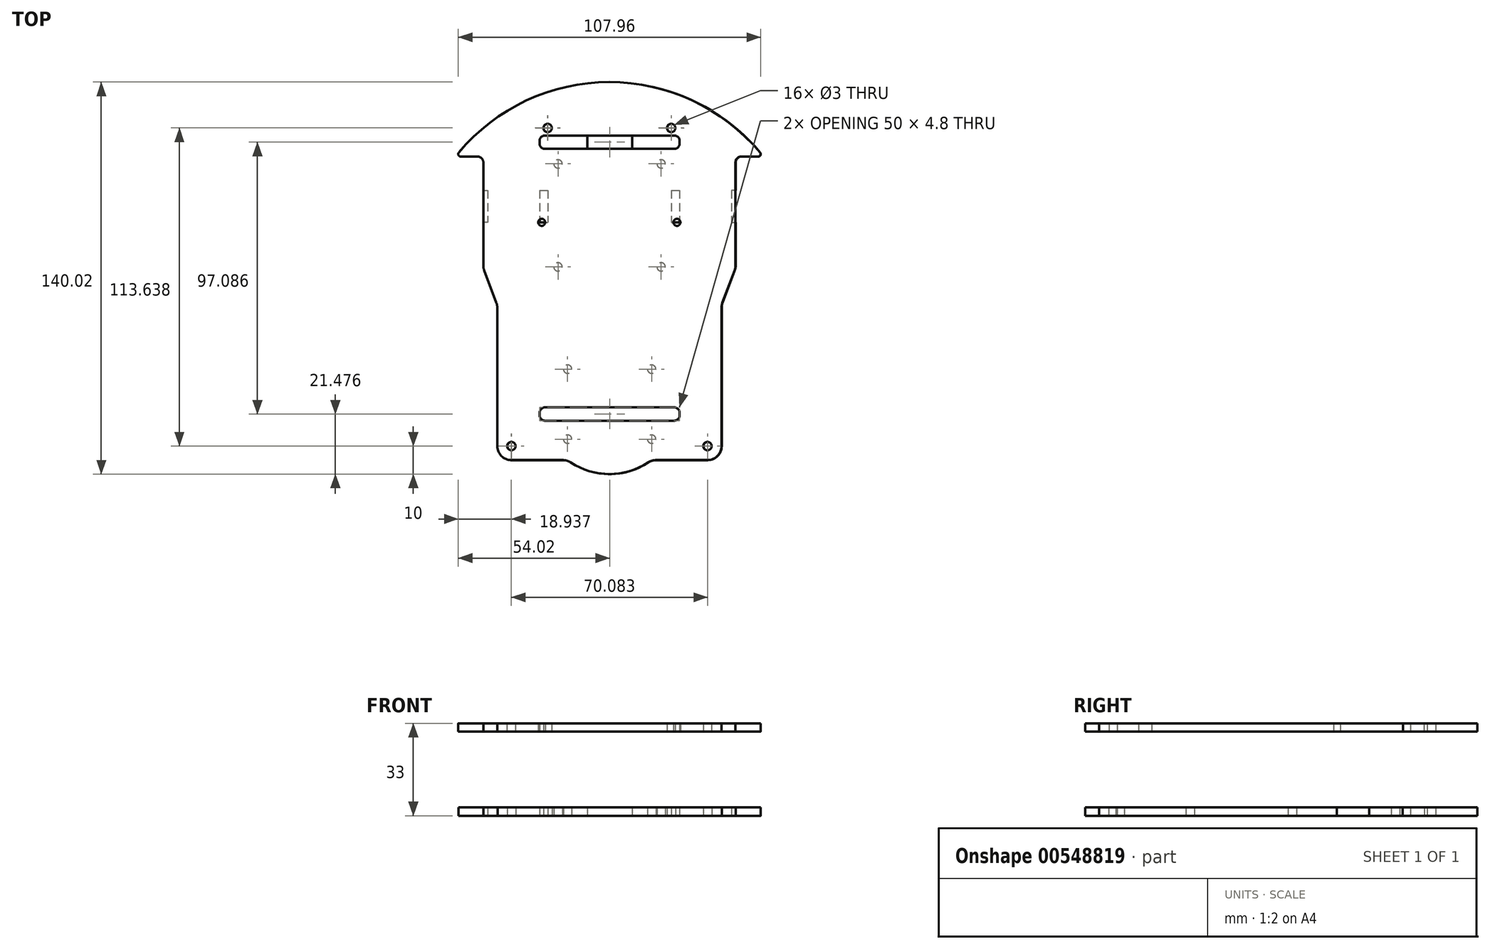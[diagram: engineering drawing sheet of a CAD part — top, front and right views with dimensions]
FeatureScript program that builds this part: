
annotation { "Feature Type Name" : "Feature", "Feature Type Description" : "" }
export const myFeature = defineFeature(function(context is Context, id is Id, definition is map)
    precondition{}
    {
        {
            var Q0;
            Q0=qCreatedBy(makeId("Top.planeOp"),FACE);
            var sketch = newSketch(context, id + "F0", { "sketchPlane" : qUnion([Q0])});
            skArc(sketch, "E0", {"start": v(53.73, 44.87) * mm, "mid": v(0, 70) * mm, "end": v(-53.73, 44.87) * mm});
            skLineSegment(sketch, "E1", {"start": v(-45, 71.35) * mm, "end": v(-45, 53.62) * mm, "construction": true});
            skLineSegment(sketch, "E2", {"start": v(-44.93, -66.83) * mm, "end": v(45.07, -66.83) * mm, "construction": true});
            skLineSegment(sketch, "E3", {"start": v(45, 4.53) * mm, "end": v(45, 19.9) * mm, "construction": true});
            skArc(sketch, "E4", {"start": v(-13.82, -65.83) * mm, "mid": v(0, -70) * mm, "end": v(13.82, -65.83) * mm});
            skLineSegment(sketch, "E5", {"start": v(-45, 53.62) * mm, "end": v(45, 53.62) * mm, "construction": true});
            skLineSegment(sketch, "E6", {"start": v(84.91, 3.62) * mm, "end": v(-92.34, 3.62) * mm, "construction": true});
            skLineSegment(sketch, "E7", {"start": v(-54.93, 66.8) * mm, "end": v(-54.93, -70.54) * mm, "construction": true});
            skLineSegment(sketch, "E8", {"start": v(55, 69.5) * mm, "end": v(55, -68.16) * mm, "construction": true});
            skLineSegment(sketch, "E9", {"start": v(-53.04, 43.4) * mm, "end": v(-47, 43.4) * mm});
            skLineSegment(sketch, "E10", {"start": v(-44.68, 2.77) * mm, "end": v(-40.32, -8.82) * mm});
            skLineSegment(sketch, "E11", {"start": v(40.32, -8.82) * mm, "end": v(44.68, 2.77) * mm});
            skLineSegment(sketch, "E12", {"start": v(45, 43.4) * mm, "end": v(45, 31.4) * mm});
            skLineSegment(sketch, "E13", {"start": v(-45, 3.62) * mm, "end": v(-45, 19.9) * mm});
            skLineSegment(sketch, "E14.trimOffspring", {"start": v(47, 43.4) * mm, "end": v(53.04, 43.4) * mm});
            skLineSegment(sketch, "E15.trimOffspring", {"start": v(-45, 41.4) * mm, "end": v(-45, 31.4) * mm, "construction": true});
            skLineSegment(sketch, "E16", {"start": v(68.52, 31.4) * mm, "end": v(-73.16, 31.4) * mm, "construction": true});
            skLineSegment(sketch, "E17", {"start": v(-80.27, 19.9) * mm, "end": v(70.38, 19.9) * mm, "construction": true});
            skLineSegment(sketch, "E18", {"start": v(-43.5, 37.52) * mm, "end": v(-43.5, 12.77) * mm, "construction": true});
            skLineSegment(sketch, "E19", {"start": v(43.5, 37.52) * mm, "end": v(43.5, 11.84) * mm, "construction": true});
            skLineSegment(sketch, "E20", {"start": v(-45, 31.4) * mm, "end": v(-43.5, 31.4) * mm});
            skLineSegment(sketch, "E21", {"start": v(-43.5, 31.4) * mm, "end": v(-43.5, 19.9) * mm});
            skLineSegment(sketch, "E22", {"start": v(-43.5, 19.9) * mm, "end": v(-45, 19.9) * mm});
            skLineSegment(sketch, "E23.trimOffspring", {"start": v(-45, 19.9) * mm, "end": v(-45, 4.53) * mm, "construction": true});
            skLineSegment(sketch, "E24.trimOffspring", {"start": v(-45, 31.4) * mm, "end": v(-45, 43.4) * mm});
            skLineSegment(sketch, "E25", {"start": v(45, 31.4) * mm, "end": v(43.5, 31.4) * mm});
            skLineSegment(sketch, "E26", {"start": v(43.5, 31.4) * mm, "end": v(43.5, 19.9) * mm});
            skLineSegment(sketch, "E27", {"start": v(43.5, 19.9) * mm, "end": v(45, 19.9) * mm});
            skLineSegment(sketch, "E28.trimOffspring", {"start": v(45, 31.4) * mm, "end": v(45, 41.4) * mm, "construction": true});
            skLineSegment(sketch, "E29.trimOffspring", {"start": v(45, 19.9) * mm, "end": v(45, 3.62) * mm});
            skLineSegment(sketch, "E30", {"start": v(-24.9, 37.4) * mm, "end": v(-24.9, 9.84) * mm, "construction": true});
            skPoint(sketch, "E30.startSnap0", {"position": v(-45, 37.4) * mm});
            skLineSegment(sketch, "E31", {"start": v(-24.9, 9.84) * mm, "end": v(24.9, 9.84) * mm, "construction": true});
            skLineSegment(sketch, "E32", {"start": v(24.9, 9.84) * mm, "end": v(24.9, 37.52) * mm, "construction": true});
            skLineSegment(sketch, "E33", {"start": v(-22, 37.06) * mm, "end": v(-22, 13.24) * mm, "construction": true});
            skLineSegment(sketch, "E34", {"start": v(-22, 13.24) * mm, "end": v(22, 13.24) * mm, "construction": true});
            skLineSegment(sketch, "E35", {"start": v(22, 13.24) * mm, "end": v(22, 38.3) * mm, "construction": true});
            skLineSegment(sketch, "E36.bottom", {"start": v(-24.9, 31.4) * mm, "end": v(-22, 31.4) * mm});
            skLineSegment(sketch, "E36.top", {"start": v(-24.9, 19.9) * mm, "end": v(-22, 19.9) * mm});
            skLineSegment(sketch, "E36.left", {"start": v(-24.9, 31.4) * mm, "end": v(-24.9, 19.9) * mm});
            skLineSegment(sketch, "E36.right", {"start": v(-22, 31.4) * mm, "end": v(-22, 19.9) * mm});
            skLineSegment(sketch, "E37.bottom", {"start": v(22, 31.4) * mm, "end": v(24.9, 31.4) * mm});
            skLineSegment(sketch, "E37.top", {"start": v(22, 19.9) * mm, "end": v(24.9, 19.9) * mm});
            skLineSegment(sketch, "E37.left", {"start": v(22, 31.4) * mm, "end": v(22, 19.9) * mm});
            skLineSegment(sketch, "E37.right", {"start": v(24.9, 31.4) * mm, "end": v(24.9, 19.9) * mm});
            skPoint(sketch, "E38.oppositeSnap0", {"position": v(22, 25.77) * mm});
            skLineSegment(sketch, "E38.left", {"start": v(22, 25.77) * mm, "end": v(22, 25.77) * mm});
            skLineSegment(sketch, "E38.right", {"start": v(-22, 25.77) * mm, "end": v(-22, 25.77) * mm});
            skLineSegment(sketch, "E39.bottom", {"start": v(-8, 51.14) * mm, "end": v(8, 51.14) * mm});
            skLineSegment(sketch, "E39.top", {"start": v(-8, 46.14) * mm, "end": v(8, 46.14) * mm});
            skLineSegment(sketch, "E39.left", {"start": v(-8, 51.14) * mm, "end": v(-8, 46.14) * mm});
            skLineSegment(sketch, "E39.right", {"start": v(8, 51.14) * mm, "end": v(8, 46.14) * mm});
            skCircle(sketch, "E40", {"center": v(18.4, 40.8) * mm, "radius": 1.5 * mm});
            skCircle(sketch, "E41.MirrorC", {"center": v(-18.4, 40.8) * mm, "radius": 1.5 * mm});
            skCircle(sketch, "E42", {"center": v(18.4, 4) * mm, "radius": 1.5 * mm});
            skLineSegment(sketch, "E43", {"start": v(18.4, 40.8) * mm, "end": v(18.4, -27.62) * mm, "construction": true});
            skCircle(sketch, "E44.MirrorC", {"center": v(-18.4, 4) * mm, "radius": 1.5 * mm});
            skLineSegment(sketch, "E45.top", {"start": v(-35, -65) * mm, "end": v(-16.58, -65) * mm});
            skLineSegment(sketch, "E45.left", {"start": v(-40, -10.58) * mm, "end": v(-40, -60) * mm});
            skLineSegment(sketch, "E45.right", {"start": v(40, -10.58) * mm, "end": v(40, -60) * mm});
            skLineSegment(sketch, "E46.trimOffspring", {"start": v(16.58, -65) * mm, "end": v(35, -65) * mm});
            skLineSegment(sketch, "E47", {"start": v(-63.48, 0) * mm, "end": v(68.67, 0) * mm, "construction": true});
            skPoint(sketch, "E48.visualSharp", {"position": v(-40, -65) * mm});
            skArc(sketch, "E48.filletArc", {"start": v(-40, -60) * mm, "mid": v(-38.54, -63.54) * mm, "end": v(-35, -65) * mm});
            skPoint(sketch, "E49.visualSharp", {"position": v(40, -65) * mm});
            skArc(sketch, "E49.filletArc", {"start": v(35, -65) * mm, "mid": v(38.54, -63.54) * mm, "end": v(40, -60) * mm});
            skPoint(sketch, "E50.visualSharp", {"position": v(15, -65) * mm});
            skArc(sketch, "E50.filletArc", {"start": v(16.58, -65) * mm, "mid": v(15.14, -65.21) * mm, "end": v(13.82, -65.83) * mm});
            skPoint(sketch, "E51.visualSharp", {"position": v(-15, -65) * mm});
            skArc(sketch, "E51.filletArc", {"start": v(-13.82, -65.83) * mm, "mid": v(-15.14, -65.21) * mm, "end": v(-16.58, -65) * mm});
            skArc(sketch, "E52.filletArc", {"start": v(-45, 4.53) * mm, "mid": v(-44.92, 3.63) * mm, "end": v(-44.68, 2.77) * mm});
            skArc(sketch, "E53.filletArc", {"start": v(44.68, 2.77) * mm, "mid": v(44.92, 3.63) * mm, "end": v(45, 4.53) * mm});
            skPoint(sketch, "E54.visualSharp", {"position": v(40, -9.67) * mm});
            skArc(sketch, "E54.filletArc", {"start": v(40.32, -8.82) * mm, "mid": v(40.08, -9.69) * mm, "end": v(40, -10.58) * mm});
            skPoint(sketch, "E55.visualSharp", {"position": v(-40, -9.67) * mm});
            skArc(sketch, "E55.filletArc", {"start": v(-40, -10.58) * mm, "mid": v(-40.08, -9.69) * mm, "end": v(-40.32, -8.82) * mm});
            skPoint(sketch, "E56.visualSharp", {"position": v(-54.93, 43.4) * mm});
            skArc(sketch, "E56.filletArc", {"start": v(-53.73, 44.87) * mm, "mid": v(-53.85, 43.91) * mm, "end": v(-53.04, 43.4) * mm});
            skPoint(sketch, "E57.visualSharp", {"position": v(54.93, 43.4) * mm});
            skArc(sketch, "E57.filletArc", {"start": v(53.04, 43.4) * mm, "mid": v(53.85, 43.91) * mm, "end": v(53.73, 44.87) * mm});
            skPoint(sketch, "E58.visualSharp", {"position": v(-45, 43.4) * mm});
            skArc(sketch, "E58.filletArc", {"start": v(-45, 41.4) * mm, "mid": v(-45.59, 42.8) * mm, "end": v(-47, 43.4) * mm});
            skArc(sketch, "E59.filletArc", {"start": v(47, 43.4) * mm, "mid": v(45.59, 42.8) * mm, "end": v(45, 41.4) * mm});
            skCircle(sketch, "E60", {"center": v(-35, -60) * mm, "radius": 1.5 * mm});
            skCircle(sketch, "E61.MirrorC", {"center": v(35, -60) * mm, "radius": 1.5 * mm});
            skCircle(sketch, "E62", {"center": v(-22.05, 53.62) * mm, "radius": 1.5 * mm});
            skCircle(sketch, "E63.MirrorC", {"center": v(22.05, 53.62) * mm, "radius": 1.5 * mm});
            skCircle(sketch, "E64", {"center": v(15, -32.5) * mm, "radius": 1.5 * mm});
            skCircle(sketch, "E65", {"center": v(15, -57.5) * mm, "radius": 1.5 * mm});
            skCircle(sketch, "E66.MirrorC", {"center": v(-15, -32.5) * mm, "radius": 1.5 * mm});
            skCircle(sketch, "E67.MirrorC", {"center": v(-15, -57.5) * mm, "radius": 1.5 * mm});
            skSolve(sketch);
        }
        {
            var Q0;
            Q0=makeQuery(id+"F0.imprint","IMPRINT",FACE,{"disambiguationData":[TD([[makeQuery(id+"F0.imprint","IMPRINT",EDGE,{"derivedFrom":sQuery(id+"F0.wireOp",EDGE,"E0")}),1.0]])]});
            extrude(context, id + "F1", {"entities" : qUnion([Q0]), "depth" : 3 * mm, "offsetDistance" : 25 * mm});
        }
        {
            var Q0;
            Q0=makeQuery(id+"F1.opExtrude","SWEPT_BODY",BODY,{"disambiguationData":[OSD([sQuery(id+"F0.wireOp",EDGE,"E0"),sQuery(id+"F0.wireOp",EDGE,"E4"),sQuery(id+"F0.wireOp",EDGE,"E9"),sQuery(id+"F0.wireOp",EDGE,"E10"),sQuery(id+"F0.wireOp",EDGE,"E11"),sQuery(id+"F0.wireOp",EDGE,"E12"),sQuery(id+"F0.wireOp",EDGE,"E13"),sQuery(id+"F0.wireOp",EDGE,"E14.trimOffspring"),sQuery(id+"F0.wireOp",EDGE,"E20"),sQuery(id+"F0.wireOp",EDGE,"E21"),sQuery(id+"F0.wireOp",EDGE,"E22"),sQuery(id+"F0.wireOp",EDGE,"E24.trimOffspring"),sQuery(id+"F0.wireOp",EDGE,"E25"),sQuery(id+"F0.wireOp",EDGE,"E26"),sQuery(id+"F0.wireOp",EDGE,"E27"),sQuery(id+"F0.wireOp",EDGE,"E29.trimOffspring"),sQuery(id+"F0.wireOp",EDGE,"E36.bottom"),sQuery(id+"F0.wireOp",EDGE,"E36.top"),sQuery(id+"F0.wireOp",EDGE,"E36.left"),sQuery(id+"F0.wireOp",EDGE,"E36.right"),sQuery(id+"F0.wireOp",EDGE,"E37.bottom"),sQuery(id+"F0.wireOp",EDGE,"E37.top"),sQuery(id+"F0.wireOp",EDGE,"E37.left"),sQuery(id+"F0.wireOp",EDGE,"E37.right"),sQuery(id+"F0.wireOp",EDGE,"E39.bottom"),sQuery(id+"F0.wireOp",EDGE,"E39.top"),sQuery(id+"F0.wireOp",EDGE,"E39.left"),sQuery(id+"F0.wireOp",EDGE,"E39.right"),sQuery(id+"F0.wireOp",EDGE,"E40"),sQuery(id+"F0.wireOp",EDGE,"E41.MirrorC"),sQuery(id+"F0.wireOp",EDGE,"E42"),sQuery(id+"F0.wireOp",EDGE,"E44.MirrorC"),sQuery(id+"F0.wireOp",EDGE,"E45.top"),sQuery(id+"F0.wireOp",EDGE,"E45.left"),sQuery(id+"F0.wireOp",EDGE,"E45.right"),sQuery(id+"F0.wireOp",EDGE,"E46.trimOffspring"),sQuery(id+"F0.wireOp",EDGE,"E48.filletArc"),sQuery(id+"F0.wireOp",EDGE,"E49.filletArc"),sQuery(id+"F0.wireOp",EDGE,"E50.filletArc"),sQuery(id+"F0.wireOp",EDGE,"E51.filletArc"),sQuery(id+"F0.wireOp",EDGE,"E52.filletArc"),sQuery(id+"F0.wireOp",EDGE,"E53.filletArc"),sQuery(id+"F0.wireOp",EDGE,"E54.filletArc"),sQuery(id+"F0.wireOp",EDGE,"E55.filletArc"),sQuery(id+"F0.wireOp",EDGE,"E56.filletArc"),sQuery(id+"F0.wireOp",EDGE,"E57.filletArc"),sQuery(id+"F0.wireOp",EDGE,"E58.filletArc"),sQuery(id+"F0.wireOp",EDGE,"E59.filletArc"),sQuery(id+"F0.wireOp",EDGE,"E60"),sQuery(id+"F0.wireOp",EDGE,"E61.MirrorC"),sQuery(id+"F0.wireOp",EDGE,"E62"),sQuery(id+"F0.wireOp",EDGE,"E63.MirrorC")])]});
            transform(context, id + "F2", {"entities" : qUnion([Q0]), "transformType" : TransformType.TRANSLATION_3D, "dx" : 0 * mm, "dy" : 0 * mm, "dz" : 30 * mm, "makeCopy" : true});
        }
        {
            var Q0;
            Q0=makeQuery(id+"F2.opPattern","COPY",BODY,{"derivedFrom":makeQuery(id+"F1.opExtrude","SWEPT_BODY",BODY,{"disambiguationData":[OSD([sQuery(id+"F0.wireOp",EDGE,"E0"),sQuery(id+"F0.wireOp",EDGE,"E4"),sQuery(id+"F0.wireOp",EDGE,"E9"),sQuery(id+"F0.wireOp",EDGE,"E10"),sQuery(id+"F0.wireOp",EDGE,"E11"),sQuery(id+"F0.wireOp",EDGE,"E12"),sQuery(id+"F0.wireOp",EDGE,"E13"),sQuery(id+"F0.wireOp",EDGE,"E14.trimOffspring"),sQuery(id+"F0.wireOp",EDGE,"E20"),sQuery(id+"F0.wireOp",EDGE,"E21"),sQuery(id+"F0.wireOp",EDGE,"E22"),sQuery(id+"F0.wireOp",EDGE,"E24.trimOffspring"),sQuery(id+"F0.wireOp",EDGE,"E25"),sQuery(id+"F0.wireOp",EDGE,"E26"),sQuery(id+"F0.wireOp",EDGE,"E27"),sQuery(id+"F0.wireOp",EDGE,"E29.trimOffspring"),sQuery(id+"F0.wireOp",EDGE,"E36.bottom"),sQuery(id+"F0.wireOp",EDGE,"E36.top"),sQuery(id+"F0.wireOp",EDGE,"E36.left"),sQuery(id+"F0.wireOp",EDGE,"E36.right"),sQuery(id+"F0.wireOp",EDGE,"E37.bottom"),sQuery(id+"F0.wireOp",EDGE,"E37.top"),sQuery(id+"F0.wireOp",EDGE,"E37.left"),sQuery(id+"F0.wireOp",EDGE,"E37.right"),sQuery(id+"F0.wireOp",EDGE,"E39.bottom"),sQuery(id+"F0.wireOp",EDGE,"E39.top"),sQuery(id+"F0.wireOp",EDGE,"E39.left"),sQuery(id+"F0.wireOp",EDGE,"E39.right"),sQuery(id+"F0.wireOp",EDGE,"E40"),sQuery(id+"F0.wireOp",EDGE,"E41.MirrorC"),sQuery(id+"F0.wireOp",EDGE,"E42"),sQuery(id+"F0.wireOp",EDGE,"E44.MirrorC"),sQuery(id+"F0.wireOp",EDGE,"E45.top"),sQuery(id+"F0.wireOp",EDGE,"E45.left"),sQuery(id+"F0.wireOp",EDGE,"E45.right"),sQuery(id+"F0.wireOp",EDGE,"E46.trimOffspring"),sQuery(id+"F0.wireOp",EDGE,"E48.filletArc"),sQuery(id+"F0.wireOp",EDGE,"E49.filletArc"),sQuery(id+"F0.wireOp",EDGE,"E50.filletArc"),sQuery(id+"F0.wireOp",EDGE,"E51.filletArc"),sQuery(id+"F0.wireOp",EDGE,"E52.filletArc"),sQuery(id+"F0.wireOp",EDGE,"E53.filletArc"),sQuery(id+"F0.wireOp",EDGE,"E54.filletArc"),sQuery(id+"F0.wireOp",EDGE,"E55.filletArc"),sQuery(id+"F0.wireOp",EDGE,"E56.filletArc"),sQuery(id+"F0.wireOp",EDGE,"E57.filletArc"),sQuery(id+"F0.wireOp",EDGE,"E58.filletArc"),sQuery(id+"F0.wireOp",EDGE,"E59.filletArc"),sQuery(id+"F0.wireOp",EDGE,"E60"),sQuery(id+"F0.wireOp",EDGE,"E61.MirrorC"),sQuery(id+"F0.wireOp",EDGE,"E62"),sQuery(id+"F0.wireOp",EDGE,"E63.MirrorC"),sQuery(id+"F0.wireOp",EDGE,"EL6qEeym-JVaA-pGui-gBE9-t7VXLs2ASFL7.bottom"),sQuery(id+"F0.wireOp",EDGE,"EL6qEeym-JVaA-pGui-gBE9-t7VXLs2ASFL7.top"),sQuery(id+"F0.wireOp",EDGE,"EL6qEeym-JVaA-pGui-gBE9-t7VXLs2ASFL7.left"),sQuery(id+"F0.wireOp",EDGE,"EL6qEeym-JVaA-pGui-gBE9-t7VXLs2ASFL7.right")])]}),"instanceName":"1"});
            deleteBodies(context, id + "F3", {"entities" : qUnion([Q0])});
        }
        {
            var Q0;
            Q0=qCreatedBy(makeId("Top.planeOp"),FACE);
            cPlane(context, id + "F4", {"entities" : qUnion([Q0]), "cplaneType" : CPlaneType.OFFSET, "offset" : 30 * mm, "width" : 150 * mm, "height" : 150 * mm});
        }
        {
            var Q0;
            Q0=qCreatedBy(id+"F4.planeOp",FACE);
            var sketch = newSketch(context, id + "F5", { "sketchPlane" : qUnion([Q0])});
            skArc(sketch, "E68", {"start": v(53.65, 44.89) * mm, "mid": v(-0.08, 70.02) * mm, "end": v(-53.81, 44.89) * mm});
            skLineSegment(sketch, "E69", {"start": v(-45.08, 62.38) * mm, "end": v(-45.08, 53.64) * mm, "construction": true});
            skLineSegment(sketch, "E70", {"start": v(-45.01, -66.81) * mm, "end": v(46.64, -66.81) * mm, "construction": true});
            skLineSegment(sketch, "E71", {"start": v(44.92, 4.55) * mm, "end": v(44.92, 19.91) * mm, "construction": true});
            skArc(sketch, "E72", {"start": v(-13.9, -65.81) * mm, "mid": v(-0.08, -69.98) * mm, "end": v(13.74, -65.81) * mm});
            skLineSegment(sketch, "E73", {"start": v(-45.08, 53.64) * mm, "end": v(44.92, 53.64) * mm, "construction": true});
            skLineSegment(sketch, "E74", {"start": v(84.83, 3.64) * mm, "end": v(-92.42, 3.64) * mm, "construction": true});
            skLineSegment(sketch, "E75", {"start": v(-55.01, 66.82) * mm, "end": v(-55.01, -70.52) * mm, "construction": true});
            skLineSegment(sketch, "E76", {"start": v(54.92, 69.52) * mm, "end": v(54.92, -68.14) * mm, "construction": true});
            skLineSegment(sketch, "E77", {"start": v(-53.12, 43.41) * mm, "end": v(-47.08, 43.41) * mm});
            skLineSegment(sketch, "E78", {"start": v(-44.76, 2.79) * mm, "end": v(-40.4, -8.8) * mm});
            skLineSegment(sketch, "E79", {"start": v(40.24, -8.8) * mm, "end": v(44.6, 2.79) * mm});
            skLineSegment(sketch, "E80", {"start": v(-45.08, -5.35) * mm, "end": v(-45.08, 41.41) * mm});
            skLineSegment(sketch, "E81.trimOffspring", {"start": v(46.92, 43.41) * mm, "end": v(52.96, 43.41) * mm});
            skLineSegment(sketch, "E82.trimOffspring", {"start": v(-45.08, 41.41) * mm, "end": v(-45.08, 4.55) * mm, "construction": true});
            skLineSegment(sketch, "E83.trimOffspring", {"start": v(44.92, 19.91) * mm, "end": v(44.92, -5.35) * mm});
            skLineSegment(sketch, "E84", {"start": v(-24.98, 9.86) * mm, "end": v(24.82, 9.86) * mm, "construction": true});
            skLineSegment(sketch, "E85.bottom", {"start": v(-23, 50.96) * mm, "end": v(23, 50.96) * mm});
            skLineSegment(sketch, "E85.top", {"start": v(-23, 46.16) * mm, "end": v(23, 46.16) * mm});
            skLineSegment(sketch, "E85.left", {"start": v(-25, 48.96) * mm, "end": v(-25, 48.16) * mm});
            skLineSegment(sketch, "E85.right", {"start": v(25, 48.96) * mm, "end": v(25, 48.16) * mm});
            skLineSegment(sketch, "E86.top", {"start": v(-35.08, -64.98) * mm, "end": v(-16.67, -64.98) * mm});
            skLineSegment(sketch, "E86.left", {"start": v(-40.08, -10.56) * mm, "end": v(-40.08, -59.98) * mm});
            skLineSegment(sketch, "E86.right", {"start": v(39.92, -10.56) * mm, "end": v(39.92, -59.98) * mm});
            skLineSegment(sketch, "E87.trimOffspring", {"start": v(16.5, -64.98) * mm, "end": v(34.92, -64.98) * mm});
            skLineSegment(sketch, "E88", {"start": v(-61.9, 0.02) * mm, "end": v(70.23, 0.02) * mm, "construction": true});
            skPoint(sketch, "E89.visualSharp", {"position": v(-40.08, -64.98) * mm});
            skArc(sketch, "E89.filletArc", {"start": v(-40.08, -59.98) * mm, "mid": v(-38.62, -63.52) * mm, "end": v(-35.08, -64.98) * mm});
            skPoint(sketch, "E90.visualSharp", {"position": v(39.92, -64.98) * mm});
            skArc(sketch, "E90.filletArc", {"start": v(34.92, -64.98) * mm, "mid": v(38.45, -63.52) * mm, "end": v(39.92, -59.98) * mm});
            skPoint(sketch, "E91.visualSharp", {"position": v(14.92, -64.98) * mm});
            skArc(sketch, "E91.filletArc", {"start": v(16.5, -64.98) * mm, "mid": v(15.06, -65.2) * mm, "end": v(13.74, -65.81) * mm});
            skPoint(sketch, "E92.visualSharp", {"position": v(-15.08, -64.98) * mm});
            skArc(sketch, "E92.filletArc", {"start": v(-13.9, -65.81) * mm, "mid": v(-15.22, -65.2) * mm, "end": v(-16.67, -64.98) * mm});
            skArc(sketch, "E93.filletArc", {"start": v(-45.08, 4.55) * mm, "mid": v(-45, 3.65) * mm, "end": v(-44.76, 2.79) * mm});
            skArc(sketch, "E94.filletArc", {"start": v(44.6, 2.79) * mm, "mid": v(44.84, 3.65) * mm, "end": v(44.92, 4.55) * mm});
            skPoint(sketch, "E95.visualSharp", {"position": v(39.92, -9.65) * mm});
            skArc(sketch, "E95.filletArc", {"start": v(40.24, -8.8) * mm, "mid": v(40, -9.67) * mm, "end": v(39.92, -10.56) * mm});
            skPoint(sketch, "E96.visualSharp", {"position": v(-40.08, -9.65) * mm});
            skArc(sketch, "E96.filletArc", {"start": v(-40.08, -10.56) * mm, "mid": v(-40.16, -9.67) * mm, "end": v(-40.4, -8.8) * mm});
            skPoint(sketch, "E97.visualSharp", {"position": v(-55.01, 43.41) * mm});
            skArc(sketch, "E97.filletArc", {"start": v(-53.81, 44.89) * mm, "mid": v(-53.94, 43.93) * mm, "end": v(-53.12, 43.41) * mm});
            skPoint(sketch, "E98.visualSharp", {"position": v(54.85, 43.41) * mm});
            skArc(sketch, "E98.filletArc", {"start": v(52.96, 43.41) * mm, "mid": v(53.77, 43.93) * mm, "end": v(53.65, 44.89) * mm});
            skPoint(sketch, "E99.visualSharp", {"position": v(-45.08, 43.41) * mm});
            skArc(sketch, "E99.filletArc", {"start": v(-45.08, 41.41) * mm, "mid": v(-45.67, 42.82) * mm, "end": v(-47.08, 43.41) * mm});
            skArc(sketch, "E100.filletArc", {"start": v(46.92, 43.41) * mm, "mid": v(45.5, 42.82) * mm, "end": v(44.92, 41.41) * mm});
            skCircle(sketch, "E101", {"center": v(-35.08, -59.98) * mm, "radius": 1.5 * mm});
            skCircle(sketch, "E102.MirrorC", {"center": v(34.92, -59.98) * mm, "radius": 1.5 * mm});
            skCircle(sketch, "E103", {"center": v(-22.13, 53.64) * mm, "radius": 1.5 * mm});
            skCircle(sketch, "E104.MirrorC", {"center": v(21.97, 53.64) * mm, "radius": 1.5 * mm});
            skLineSegment(sketch, "E105", {"start": v(44.92, 41.41) * mm, "end": v(44.92, 19.91) * mm});
            skLineSegment(sketch, "E106.bottom", {"start": v(-26.72, 35.22) * mm, "end": v(26.62, 35.22) * mm, "construction": true});
            skLineSegment(sketch, "E106.top", {"start": v(-26.72, -33.58) * mm, "end": v(26.62, -33.58) * mm, "construction": true});
            skLineSegment(sketch, "E106.left", {"start": v(-26.72, 35.22) * mm, "end": v(-26.72, -33.58) * mm, "construction": true});
            skLineSegment(sketch, "E106.right", {"start": v(26.62, 35.22) * mm, "end": v(26.62, -33.58) * mm, "construction": true});
            skLineSegment(sketch, "E107", {"start": v(33.93, 19.92) * mm, "end": v(-36, 19.92) * mm, "construction": true});
            skLineSegment(sketch, "E108", {"start": v(-24.22, 39.52) * mm, "end": v(-24.22, -46.79) * mm, "construction": true});
            skCircle(sketch, "E109", {"center": v(-24.22, 19.92) * mm, "radius": 1.25 * mm});
            skCircle(sketch, "E110", {"center": v(24.04, 19.92) * mm, "radius": 1.25 * mm});
            skLineSegment(sketch, "E111", {"start": v(0, 61.32) * mm, "end": v(0, 37.65) * mm, "construction": true});
            skPoint(sketch, "E112.visualSharp", {"position": v(-25, 50.96) * mm});
            skArc(sketch, "E112.filletArc", {"start": v(-23, 50.96) * mm, "mid": v(-24.41, 50.38) * mm, "end": v(-25, 48.96) * mm});
            skPoint(sketch, "E113.visualSharp", {"position": v(-25, 46.16) * mm});
            skArc(sketch, "E113.filletArc", {"start": v(-25, 48.16) * mm, "mid": v(-24.41, 46.75) * mm, "end": v(-23, 46.16) * mm});
            skPoint(sketch, "E114.visualSharp", {"position": v(25, 50.96) * mm});
            skArc(sketch, "E114.filletArc", {"start": v(25, 48.96) * mm, "mid": v(24.41, 50.38) * mm, "end": v(23, 50.96) * mm});
            skPoint(sketch, "E115.visualSharp", {"position": v(25, 46.16) * mm});
            skArc(sketch, "E115.filletArc", {"start": v(23, 46.16) * mm, "mid": v(24.41, 46.75) * mm, "end": v(25, 48.16) * mm});
            skLineSegment(sketch, "E116.MirrorCS", {"start": v(-23, -46.12) * mm, "end": v(23, -46.12) * mm});
            skLineSegment(sketch, "E117.MirrorCS", {"start": v(-23, -50.92) * mm, "end": v(23, -50.92) * mm});
            skPoint(sketch, "E118.MirrorP", {"position": v(-25, -50.92) * mm});
            skArc(sketch, "E119.MirrorCS", {"start": v(-25, -48.12) * mm, "mid": v(-24.41, -46.7) * mm, "end": v(-23, -46.12) * mm});
            skArc(sketch, "E120.MirrorCS", {"start": v(-23, -50.92) * mm, "mid": v(-24.41, -50.34) * mm, "end": v(-25, -48.92) * mm});
            skLineSegment(sketch, "E121.MirrorCS", {"start": v(-25, -48.92) * mm, "end": v(-25, -48.12) * mm});
            skArc(sketch, "E122.MirrorCS", {"start": v(25, -48.92) * mm, "mid": v(24.41, -50.34) * mm, "end": v(23, -50.92) * mm});
            skLineSegment(sketch, "E123.MirrorCS", {"start": v(25, -48.92) * mm, "end": v(25, -48.12) * mm});
            skArc(sketch, "E124.MirrorCS", {"start": v(23, -46.12) * mm, "mid": v(24.41, -46.7) * mm, "end": v(25, -48.12) * mm});
            skSolve(sketch);
        }
        {
            var Q0;
            Q0=makeQuery(id+"F5.imprint","IMPRINT",FACE,{"disambiguationData":[TD([[makeQuery(id+"F5.imprint","IMPRINT",EDGE,{"derivedFrom":sQuery(id+"F5.wireOp",EDGE,"E68")}),1.0]])]});
            extrude(context, id + "F6", {"entities" : qUnion([Q0]), "depth" : 3 * mm, "offsetDistance" : 25 * mm});
        }
    });
